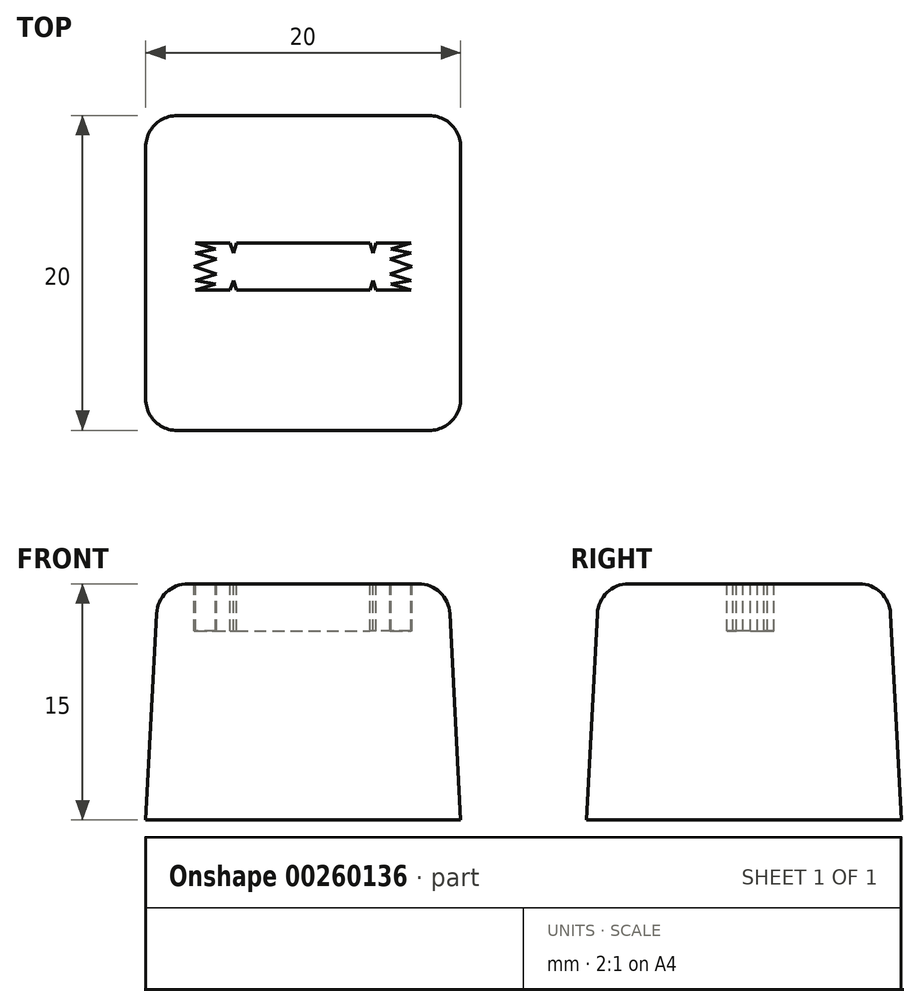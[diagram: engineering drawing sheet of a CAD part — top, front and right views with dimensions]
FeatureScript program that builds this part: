
annotation { "Feature Type Name" : "Feature", "Feature Type Description" : "" }
export const myFeature = defineFeature(function(context is Context, id is Id, definition is map)
    precondition{}
    {
        {
            var Q0;
            Q0=qCreatedBy(makeId("Top.planeOp"),FACE);
            var sketch = newSketch(context, id + "F0", { "sketchPlane" : qUnion([Q0])});
            skLineSegment(sketch, "E0.bottom", {"start": v(-8.74, 10.32) * mm, "end": v(11.26, 10.32) * mm});
            skLineSegment(sketch, "E0.top", {"start": v(-8.74, -9.68) * mm, "end": v(11.26, -9.68) * mm});
            skLineSegment(sketch, "E0.left", {"start": v(-8.74, 10.32) * mm, "end": v(-8.74, -9.68) * mm});
            skLineSegment(sketch, "E0.right", {"start": v(11.26, 10.32) * mm, "end": v(11.26, -9.68) * mm});
            skSolve(sketch);
        }
        {
            var Q0;
            Q0 = qSketchRegion(id + "F0", true);
            extrude(context, id + "F1", {"entities" : qUnion([Q0]), "depth" : 15 * mm, "hasDraft" : true, "draftAngle" : 3 * degree, "draftPullDirection" : true});
        }
        {
            var Q0;
            Q0=makeQuery(id+"F1.opExtrude","SWEPT_EDGE",EDGE,{"disambiguationData":[OSD([sQuery(id+"F0.wireOp",EDGE,"E0.bottom"),sQuery(id+"F0.wireOp",EDGE,"E0.left")])]});
            var Q1;
            Q1=makeQuery(id+"F1.opExtrude","CAP_EDGE",EDGE,{"disambiguationData":[OSD([sQuery(id+"F0.wireOp",EDGE,"E0.bottom")])],"isStart":false});
            var Q2;
            Q2=makeQuery(id+"F1.opExtrude","CAP_EDGE",EDGE,{"disambiguationData":[OSD([sQuery(id+"F0.wireOp",EDGE,"E0.right")])],"isStart":false});
            var Q3;
            Q3=makeQuery(id+"F1.opExtrude","CAP_EDGE",EDGE,{"disambiguationData":[OSD([sQuery(id+"F0.wireOp",EDGE,"E0.top")])],"isStart":false});
            var Q4;
            Q4=makeQuery(id+"F1.opExtrude","CAP_EDGE",EDGE,{"disambiguationData":[OSD([sQuery(id+"F0.wireOp",EDGE,"E0.left")])],"isStart":false});
            var Q5;
            Q5=makeQuery(id+"F1.opExtrude","SWEPT_EDGE",EDGE,{"disambiguationData":[OSD([sQuery(id+"F0.wireOp",EDGE,"E0.bottom"),sQuery(id+"F0.wireOp",EDGE,"E0.right")])]});
            var Q6;
            Q6=makeQuery(id+"F1.opExtrude","SWEPT_EDGE",EDGE,{"disambiguationData":[OSD([sQuery(id+"F0.wireOp",EDGE,"E0.top"),sQuery(id+"F0.wireOp",EDGE,"E0.right")])]});
            var Q7;
            Q7=makeQuery(id+"F1.opExtrude","SWEPT_EDGE",EDGE,{"disambiguationData":[OSD([sQuery(id+"F0.wireOp",EDGE,"E0.top"),sQuery(id+"F0.wireOp",EDGE,"E0.left")])]});
            fillet(context, id + "F2", {"entities" : qUnion([Q0, Q1, Q2, Q3, Q4, Q5, Q6, Q7]), "radius" : 2 * mm, "tangentPropagation" : true, "allowEdgeOverflow" : false});
        }
        {
            var Q0;
            Q0=makeQuery(id+"F1.opExtrude","CAP_FACE",FACE,{"disambiguationData":[OSD([sQuery(id+"F0.wireOp",EDGE,"E0.bottom"),sQuery(id+"F0.wireOp",EDGE,"E0.top"),sQuery(id+"F0.wireOp",EDGE,"E0.left"),sQuery(id+"F0.wireOp",EDGE,"E0.right")])],"isStart":false});
            var sketch = newSketch(context, id + "F3", { "sketchPlane" : qUnion([Q0])});
            skPoint(sketch, "E1.end.orphan", {"position": v(1.26, -7) * mm});
            skPoint(sketch, "E1.start.orphan", {"position": v(1.26, 7.63) * mm});
            skLineSegment(sketch, "E2", {"start": v(-5.66, 0.72) * mm, "end": v(-4.25, 1.19) * mm});
            skLineSegment(sketch, "E3", {"start": v(-4.25, 1.19) * mm, "end": v(-5.58, 1.59) * mm});
            skLineSegment(sketch, "E4", {"start": v(-5.58, 1.59) * mm, "end": v(-4.3, 1.82) * mm});
            skLineSegment(sketch, "E5", {"start": v(-4.3, 1.82) * mm, "end": v(-5.58, 2.2) * mm});
            skLineSegment(sketch, "E6", {"start": v(-5.58, 2.2) * mm, "end": v(-3.38, 2.2) * mm});
            skLineSegment(sketch, "E7", {"start": v(-3.38, 2.2) * mm, "end": v(-3.17, 1.59) * mm});
            skLineSegment(sketch, "E8", {"start": v(-3.17, 1.59) * mm, "end": v(-2.98, 2.2) * mm});
            skLineSegment(sketch, "E9", {"start": v(-2.98, 2.2) * mm, "end": v(1.26, 2.2) * mm});
            skLineSegment(sketch, "E10.MirrorCS", {"start": v(5.5, 2.2) * mm, "end": v(1.26, 2.2) * mm});
            skLineSegment(sketch, "E11.MirrorCS", {"start": v(5.7, 1.59) * mm, "end": v(5.5, 2.2) * mm});
            skLineSegment(sketch, "E12.MirrorCS", {"start": v(5.9, 2.2) * mm, "end": v(5.7, 1.59) * mm});
            skLineSegment(sketch, "E13.MirrorCS", {"start": v(8.1, 2.2) * mm, "end": v(5.9, 2.2) * mm});
            skLineSegment(sketch, "E14.MirrorCS", {"start": v(6.83, 1.82) * mm, "end": v(8.1, 2.2) * mm});
            skLineSegment(sketch, "E15.MirrorCS", {"start": v(8.1, 1.59) * mm, "end": v(6.83, 1.82) * mm});
            skLineSegment(sketch, "E16.MirrorCS", {"start": v(6.77, 1.19) * mm, "end": v(8.1, 1.59) * mm});
            skLineSegment(sketch, "E17.MirrorCS", {"start": v(8.18, 0.72) * mm, "end": v(6.77, 1.19) * mm});
            skLineSegment(sketch, "E18.MirrorCS", {"start": v(-5.66, 0.72) * mm, "end": v(-4.25, 0.25) * mm});
            skLineSegment(sketch, "E19.MirrorCS", {"start": v(-4.25, 0.25) * mm, "end": v(-5.58, -0.15) * mm});
            skLineSegment(sketch, "E20.MirrorCS", {"start": v(-5.58, -0.15) * mm, "end": v(-4.3, -0.4) * mm});
            skLineSegment(sketch, "E21.MirrorCS", {"start": v(-4.3, -0.4) * mm, "end": v(-5.58, -0.77) * mm});
            skLineSegment(sketch, "E22.MirrorCS", {"start": v(-5.58, -0.77) * mm, "end": v(-3.38, -0.77) * mm});
            skLineSegment(sketch, "E23.MirrorCS", {"start": v(-3.38, -0.77) * mm, "end": v(-3.17, -0.15) * mm});
            skLineSegment(sketch, "E24.MirrorCS", {"start": v(-3.17, -0.15) * mm, "end": v(-2.98, -0.77) * mm});
            skLineSegment(sketch, "E25.MirrorCS", {"start": v(-2.98, -0.77) * mm, "end": v(1.26, -0.77) * mm});
            skLineSegment(sketch, "E26.MirrorCS", {"start": v(5.5, -0.77) * mm, "end": v(1.26, -0.77) * mm});
            skLineSegment(sketch, "E27.MirrorCS", {"start": v(5.7, -0.15) * mm, "end": v(5.5, -0.77) * mm});
            skLineSegment(sketch, "E28.MirrorCS", {"start": v(5.9, -0.77) * mm, "end": v(5.7, -0.15) * mm});
            skLineSegment(sketch, "E29.MirrorCS", {"start": v(8.1, -0.77) * mm, "end": v(5.9, -0.77) * mm});
            skLineSegment(sketch, "E30.MirrorCS", {"start": v(6.83, -0.4) * mm, "end": v(8.1, -0.77) * mm});
            skLineSegment(sketch, "E31.MirrorCS", {"start": v(8.1, -0.15) * mm, "end": v(6.83, -0.4) * mm});
            skLineSegment(sketch, "E32.MirrorCS", {"start": v(6.77, 0.25) * mm, "end": v(8.1, -0.15) * mm});
            skLineSegment(sketch, "E33.MirrorCS", {"start": v(8.18, 0.72) * mm, "end": v(6.77, 0.25) * mm});
            skSolve(sketch);
        }
        {
            var Q0;
            Q0 = qSketchRegion(id + "F3", true);
            extrude(context, id + "F4", {"entities" : qUnion([Q0]), "operationType" : NewBodyOperationType.REMOVE, "oppositeDirection" : true, "depth" : 3 * mm});
        }
    });
